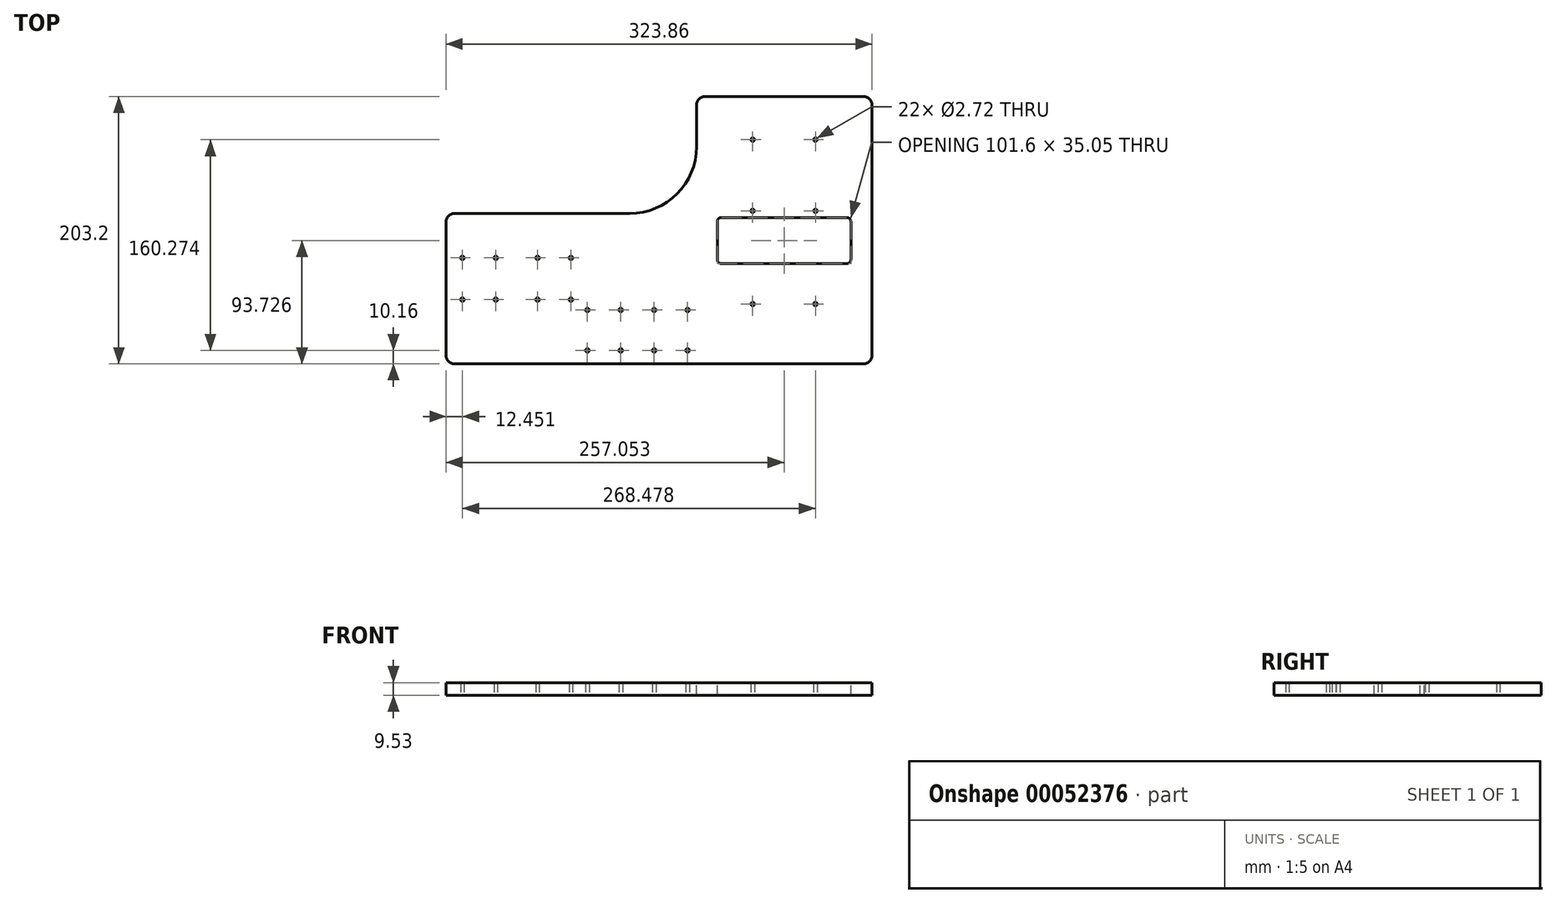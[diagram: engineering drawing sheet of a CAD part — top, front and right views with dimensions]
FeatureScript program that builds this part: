
annotation { "Feature Type Name" : "Feature", "Feature Type Description" : "" }
export const myFeature = defineFeature(function(context is Context, id is Id, definition is map)
    precondition{}
    {
        {
            var Q0;
            Q0=qCreatedBy(makeId("Top.planeOp"),FACE);
            var sketch = newSketch(context, id + "F0", { "sketchPlane" : qUnion([Q0])});
            skLineSegment(sketch, "E0", {"start": v(161.92, 95.25) * mm, "end": v(161.93, -95.25) * mm});
            skLineSegment(sketch, "E1", {"start": v(155.57, -101.6) * mm, "end": v(-155.58, -101.6) * mm});
            skLineSegment(sketch, "E2", {"start": v(-161.92, -95.25) * mm, "end": v(-161.92, 6.35) * mm});
            skLineSegment(sketch, "E3", {"start": v(-155.58, 12.7) * mm, "end": v(-22.22, 12.7) * mm});
            skLineSegment(sketch, "E4", {"start": v(28.58, 63.5) * mm, "end": v(28.58, 95.25) * mm});
            skLineSegment(sketch, "E5", {"start": v(34.93, 101.6) * mm, "end": v(155.57, 101.6) * mm});
            skPoint(sketch, "E6", {"position": v(0, -101.6) * mm});
            skPoint(sketch, "E7", {"position": v(161.92, 0) * mm});
            skPoint(sketch, "E8.visualSharp", {"position": v(28.58, 12.7) * mm});
            skArc(sketch, "E8.filletArc", {"start": v(-22.22, 12.7) * mm, "mid": v(13.7, 27.58) * mm, "end": v(28.58, 63.5) * mm});
            skPoint(sketch, "E9.visualSharp", {"position": v(161.93, -101.6) * mm});
            skArc(sketch, "E9.filletArc", {"start": v(155.57, -101.6) * mm, "mid": v(160.07, -99.74) * mm, "end": v(161.92, -95.25) * mm});
            skPoint(sketch, "E10.visualSharp", {"position": v(-161.92, -101.6) * mm});
            skArc(sketch, "E10.filletArc", {"start": v(-161.93, -95.25) * mm, "mid": v(-160.07, -99.74) * mm, "end": v(-155.58, -101.6) * mm});
            skPoint(sketch, "E11.visualSharp", {"position": v(-161.92, 12.7) * mm});
            skArc(sketch, "E11.filletArc", {"start": v(-155.58, 12.7) * mm, "mid": v(-160.07, 10.84) * mm, "end": v(-161.93, 6.35) * mm});
            skPoint(sketch, "E12.visualSharp", {"position": v(28.58, 101.6) * mm});
            skArc(sketch, "E12.filletArc", {"start": v(34.93, 101.6) * mm, "mid": v(30.43, 99.74) * mm, "end": v(28.58, 95.25) * mm});
            skPoint(sketch, "E13.visualSharp", {"position": v(161.92, 101.6) * mm});
            skArc(sketch, "E13.filletArc", {"start": v(161.92, 95.25) * mm, "mid": v(160.07, 99.74) * mm, "end": v(155.57, 101.6) * mm});
            skLineSegment(sketch, "E14.bottom", {"start": v(142.87, 9.65) * mm, "end": v(47.37, 9.65) * mm});
            skLineSegment(sketch, "E14.top", {"start": v(142.88, -25.4) * mm, "end": v(47.37, -25.4) * mm});
            skLineSegment(sketch, "E14.left", {"start": v(145.92, 6.6) * mm, "end": v(145.92, -22.35) * mm});
            skLineSegment(sketch, "E14.right", {"start": v(44.32, 6.6) * mm, "end": v(44.32, -22.35) * mm});
            skPoint(sketch, "E15.visualSharp", {"position": v(145.92, -25.4) * mm});
            skArc(sketch, "E15.filletArc", {"start": v(142.88, -25.4) * mm, "mid": v(145.03, -24.5) * mm, "end": v(145.92, -22.35) * mm});
            skPoint(sketch, "E16.visualSharp", {"position": v(44.32, -25.4) * mm});
            skArc(sketch, "E16.filletArc", {"start": v(44.32, -22.35) * mm, "mid": v(45.22, -24.5) * mm, "end": v(47.37, -25.4) * mm});
            skPoint(sketch, "E17.visualSharp", {"position": v(44.32, 9.65) * mm});
            skArc(sketch, "E17.filletArc", {"start": v(47.37, 9.65) * mm, "mid": v(45.22, 8.76) * mm, "end": v(44.32, 6.6) * mm});
            skPoint(sketch, "E18.visualSharp", {"position": v(145.92, 9.65) * mm});
            skArc(sketch, "E18.filletArc", {"start": v(145.92, 6.6) * mm, "mid": v(145.03, 8.76) * mm, "end": v(142.87, 9.65) * mm});
            skSolve(sketch);
        }
        {
            var Q0;
            Q0 = qSketchRegion(id + "F0", true);
            extrude(context, id + "F1", {"entities" : qUnion([Q0]), "oppositeDirection" : true, "depth" : 9.52 * mm});
        }
        {
            var Q0;
            Q0=qCreatedBy(makeId("Top.planeOp"),FACE);
            var sketch = newSketch(context, id + "F2", { "sketchPlane" : qUnion([Q0])});
            skPoint(sketch, "E19", {"position": v(71.25, 68.83) * mm});
            skPoint(sketch, "E20", {"position": v(119, 68.83) * mm});
            skPoint(sketch, "E21", {"position": v(119, 14.73) * mm});
            skPoint(sketch, "E22", {"position": v(71.25, 14.73) * mm});
            skPoint(sketch, "E23", {"position": v(71.25, -56.13) * mm});
            skPoint(sketch, "E24", {"position": v(119, -56.13) * mm});
            skPoint(sketch, "E25", {"position": v(-149.48, -21.08) * mm});
            skPoint(sketch, "E26", {"position": v(-149.48, -52.83) * mm});
            skPoint(sketch, "E27", {"position": v(-124.08, -21.08) * mm});
            skPoint(sketch, "E28", {"position": v(-124.08, -52.83) * mm});
            skPoint(sketch, "E29", {"position": v(-92.33, -21.08) * mm});
            skPoint(sketch, "E30", {"position": v(-92.33, -52.83) * mm});
            skPoint(sketch, "E31", {"position": v(-66.93, -21.08) * mm});
            skPoint(sketch, "E32", {"position": v(-66.93, -52.83) * mm});
            skPoint(sketch, "E33", {"position": v(-54.48, -60.7) * mm});
            skPoint(sketch, "E34", {"position": v(-54.48, -91.44) * mm});
            skPoint(sketch, "E35", {"position": v(-29.08, -60.7) * mm});
            skPoint(sketch, "E36", {"position": v(-29.08, -91.44) * mm});
            skPoint(sketch, "E37", {"position": v(-3.68, -60.7) * mm});
            skPoint(sketch, "E38", {"position": v(-3.68, -91.44) * mm});
            skPoint(sketch, "E39", {"position": v(21.72, -60.7) * mm});
            skPoint(sketch, "E40", {"position": v(21.72, -91.44) * mm});
            skSolve(sketch);
        }
        {
            var Q0;
            Q0=sQuery(id+"F2.wireOp",VERTEX,"E24");
            var Q1;
            Q1=sQuery(id+"F2.wireOp",VERTEX,"E21");
            var Q2;
            Q2=sQuery(id+"F2.wireOp",VERTEX,"E20");
            var Q3;
            Q3=sQuery(id+"F2.wireOp",VERTEX,"E19");
            var Q4;
            Q4=sQuery(id+"F2.wireOp",VERTEX,"E22");
            var Q5;
            Q5=sQuery(id+"F2.wireOp",VERTEX,"E23");
            var Q6;
            Q6=sQuery(id+"F2.wireOp",VERTEX,"E39");
            var Q7;
            Q7=sQuery(id+"F2.wireOp",VERTEX,"E40");
            var Q8;
            Q8=sQuery(id+"F2.wireOp",VERTEX,"E37");
            var Q9;
            Q9=sQuery(id+"F2.wireOp",VERTEX,"E38");
            var Q10;
            Q10=sQuery(id+"F2.wireOp",VERTEX,"E35");
            var Q11;
            Q11=sQuery(id+"F2.wireOp",VERTEX,"E36");
            var Q12;
            Q12=sQuery(id+"F2.wireOp",VERTEX,"E34");
            var Q13;
            Q13=sQuery(id+"F2.wireOp",VERTEX,"E33");
            var Q14;
            Q14=sQuery(id+"F2.wireOp",VERTEX,"E32");
            var Q15;
            Q15=sQuery(id+"F2.wireOp",VERTEX,"E31");
            var Q16;
            Q16=sQuery(id+"F2.wireOp",VERTEX,"E30");
            var Q17;
            Q17=sQuery(id+"F2.wireOp",VERTEX,"E29");
            var Q18;
            Q18=sQuery(id+"F2.wireOp",VERTEX,"E28");
            var Q19;
            Q19=sQuery(id+"F2.wireOp",VERTEX,"E27");
            var Q20;
            Q20=sQuery(id+"F2.wireOp",VERTEX,"E26");
            var Q21;
            Q21=sQuery(id+"F2.wireOp",VERTEX,"E25");
            var Q22;
            Q22=makeQuery(id+"F1.opExtrude","SWEPT_BODY",BODY,{"disambiguationData":[OSD([sQuery(id+"F0.wireOp",EDGE,"E0"),sQuery(id+"F0.wireOp",EDGE,"E1"),sQuery(id+"F0.wireOp",EDGE,"E2"),sQuery(id+"F0.wireOp",EDGE,"E3"),sQuery(id+"F0.wireOp",EDGE,"E4"),sQuery(id+"F0.wireOp",EDGE,"E5"),sQuery(id+"F0.wireOp",EDGE,"E8.filletArc"),sQuery(id+"F0.wireOp",EDGE,"E9.filletArc"),sQuery(id+"F0.wireOp",EDGE,"E10.filletArc"),sQuery(id+"F0.wireOp",EDGE,"E11.filletArc"),sQuery(id+"F0.wireOp",EDGE,"E12.filletArc"),sQuery(id+"F0.wireOp",EDGE,"E13.filletArc"),sQuery(id+"F0.wireOp",EDGE,"E14.bottom"),sQuery(id+"F0.wireOp",EDGE,"E14.top"),sQuery(id+"F0.wireOp",EDGE,"E14.left"),sQuery(id+"F0.wireOp",EDGE,"E14.right"),sQuery(id+"F0.wireOp",EDGE,"E15.filletArc"),sQuery(id+"F0.wireOp",EDGE,"E16.filletArc"),sQuery(id+"F0.wireOp",EDGE,"E17.filletArc"),sQuery(id+"F0.wireOp",EDGE,"E18.filletArc")])]});
            hole(context, id + "F3", {"style" : HoleStyle.SIMPLE, "holeDiameter" : 2.72 * mm, "endStyle" : HoleEndStyle.THROUGH, "locations" : qUnion([Q0, Q1, Q2, Q3, Q4, Q5, Q6, Q7, Q8, Q9, Q10, Q11, Q12, Q13, Q14, Q15, Q16, Q17, Q18, Q19, Q20, Q21]), "scope" : qUnion([Q22])});
        }
    });
